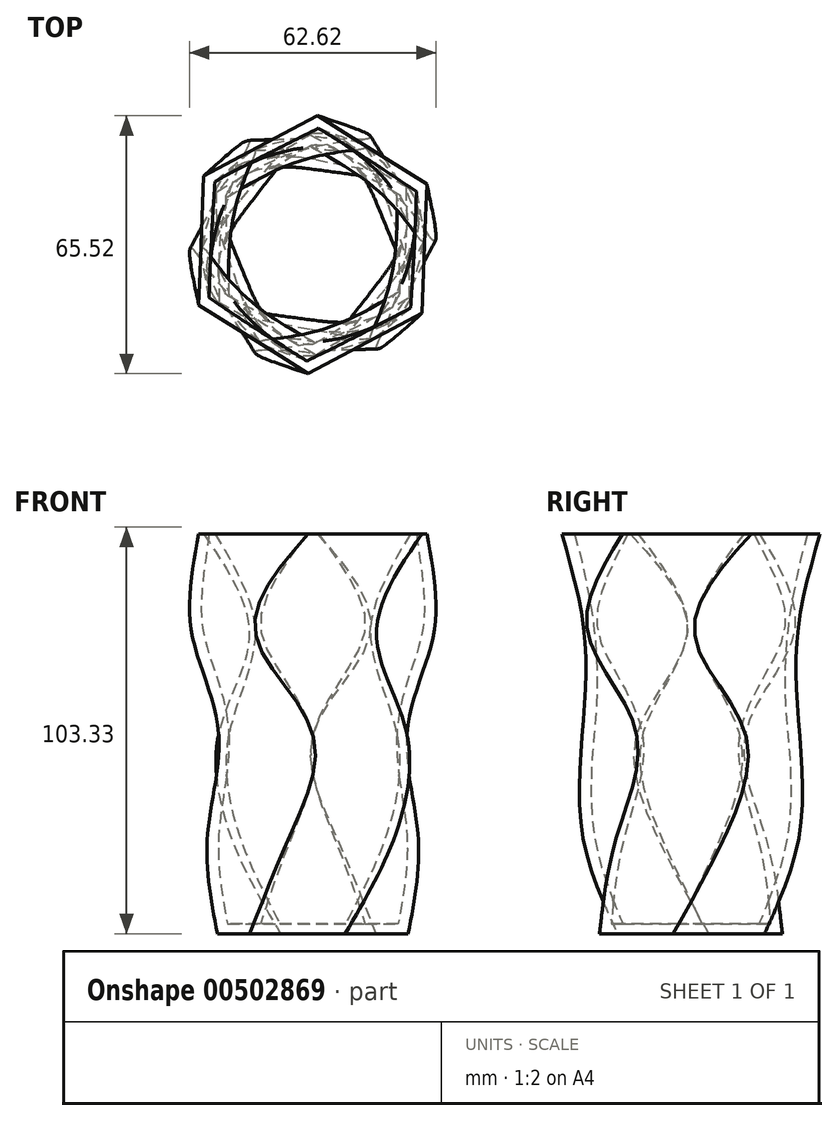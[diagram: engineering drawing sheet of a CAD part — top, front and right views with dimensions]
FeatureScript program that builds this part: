
annotation { "Feature Type Name" : "Feature", "Feature Type Description" : "" }
export const myFeature = defineFeature(function(context is Context, id is Id, definition is map)
    precondition{}
    {
        {
            var Q0;
            Q0=qCreatedBy(makeId("Top.planeOp"),FACE);
            var sketch = newSketch(context, id + "F0", { "sketchPlane" : qUnion([Q0])});
            skCircle(sketch, "E0.cCircle", {"center": v(0, 0) * mm, "radius": 21.33 * mm, "construction": true});
            skLineSegment(sketch, "E0.0", {"start": v(16.04, 18.7) * mm, "end": v(24.2, -4.54) * mm});
            skLineSegment(sketch, "E0.1", {"start": v(24.2, -4.54) * mm, "end": v(8.17, -23.23) * mm});
            skLineSegment(sketch, "E0.2", {"start": v(8.17, -23.23) * mm, "end": v(-16.04, -18.7) * mm});
            skLineSegment(sketch, "E0.3", {"start": v(-16.04, -18.7) * mm, "end": v(-24.2, 4.54) * mm});
            skLineSegment(sketch, "E0.4", {"start": v(-24.2, 4.54) * mm, "end": v(-8.17, 23.23) * mm});
            skLineSegment(sketch, "E0.5", {"start": v(-8.17, 23.23) * mm, "end": v(16.04, 18.7) * mm});
            skPoint(sketch, "E0.0.midPoint", {"position": v(20.12, 7.07) * mm});
            skSolve(sketch);
        }
        {
            var Q0;
            Q0=qCreatedBy(makeId("Top.planeOp"),FACE);
            cPlane(context, id + "F1", {"entities" : qUnion([Q0]), "cplaneType" : CPlaneType.OFFSET, "offset" : 25.4 * mm, "width" : 152.4 * mm, "height" : 152.4 * mm});
        }
        {
            var Q0;
            Q0=qCreatedBy(id+"F1.planeOp",FACE);
            var sketch = newSketch(context, id + "F2", { "sketchPlane" : qUnion([Q0])});
            skCircle(sketch, "E1.cCircle", {"center": v(0, 0) * mm, "radius": 24.38 * mm, "construction": true});
            skLineSegment(sketch, "E1.0", {"start": v(26.7, 8.92) * mm, "end": v(21.08, -18.67) * mm});
            skLineSegment(sketch, "E1.1", {"start": v(21.08, -18.67) * mm, "end": v(-5.63, -27.59) * mm});
            skLineSegment(sketch, "E1.2", {"start": v(-5.63, -27.59) * mm, "end": v(-26.7, -8.92) * mm});
            skLineSegment(sketch, "E1.3", {"start": v(-26.7, -8.92) * mm, "end": v(-21.08, 18.67) * mm});
            skLineSegment(sketch, "E1.4", {"start": v(-21.08, 18.67) * mm, "end": v(5.63, 27.59) * mm});
            skLineSegment(sketch, "E1.5", {"start": v(5.63, 27.59) * mm, "end": v(26.7, 8.92) * mm});
            skPoint(sketch, "E1.0.midPoint", {"position": v(23.9, -4.87) * mm});
            skSolve(sketch);
        }
        {
            var Q0;
            Q0=qCreatedBy(id+"F1.planeOp",FACE);
            cPlane(context, id + "F3", {"entities" : qUnion([Q0]), "cplaneType" : CPlaneType.OFFSET, "offset" : 25.4 * mm, "width" : 152.4 * mm, "height" : 152.4 * mm});
        }
        {
            var Q0;
            Q0=qCreatedBy(id+"F3.planeOp",FACE);
            var sketch = newSketch(context, id + "F4", { "sketchPlane" : qUnion([Q0])});
            skCircle(sketch, "E2.cCircle", {"center": v(0, 0) * mm, "radius": 23.9 * mm, "construction": true});
            skLineSegment(sketch, "E2.0", {"start": v(23.9, 13.8) * mm, "end": v(23.9, -13.8) * mm});
            skLineSegment(sketch, "E2.1", {"start": v(23.9, -13.8) * mm, "end": v(0, -27.59) * mm});
            skLineSegment(sketch, "E2.2", {"start": v(0, -27.59) * mm, "end": v(-23.9, -13.8) * mm});
            skLineSegment(sketch, "E2.3", {"start": v(-23.9, -13.8) * mm, "end": v(-23.9, 13.8) * mm});
            skLineSegment(sketch, "E2.4", {"start": v(-23.9, 13.8) * mm, "end": v(0, 27.59) * mm});
            skLineSegment(sketch, "E2.5", {"start": v(0, 27.59) * mm, "end": v(23.9, 13.8) * mm});
            skPoint(sketch, "E2.0.midPoint", {"position": v(23.9, 0) * mm});
            skSolve(sketch);
        }
        {
            var Q0;
            Q0=qCreatedBy(id+"F3.planeOp",FACE);
            cPlane(context, id + "F5", {"entities" : qUnion([Q0]), "cplaneType" : CPlaneType.OFFSET, "offset" : 25.4 * mm, "width" : 152.4 * mm, "height" : 152.4 * mm});
        }
        {
            var Q0;
            Q0=qCreatedBy(id+"F5.planeOp",FACE);
            var sketch = newSketch(context, id + "F6", { "sketchPlane" : qUnion([Q0])});
            skCircle(sketch, "E3.cCircle", {"center": v(0, 0) * mm, "radius": 26.6 * mm, "construction": true});
            skLineSegment(sketch, "E3.0", {"start": v(14.56, 27.06) * mm, "end": v(30.71, 0.92) * mm});
            skLineSegment(sketch, "E3.1", {"start": v(30.71, 0.92) * mm, "end": v(16.15, -26.14) * mm});
            skLineSegment(sketch, "E3.2", {"start": v(16.15, -26.14) * mm, "end": v(-14.56, -27.06) * mm});
            skLineSegment(sketch, "E3.3", {"start": v(-14.56, -27.06) * mm, "end": v(-30.71, -0.92) * mm});
            skLineSegment(sketch, "E3.4", {"start": v(-30.71, -0.92) * mm, "end": v(-16.15, 26.14) * mm});
            skLineSegment(sketch, "E3.5", {"start": v(-16.15, 26.14) * mm, "end": v(14.56, 27.06) * mm});
            skPoint(sketch, "E3.0.midPoint", {"position": v(22.64, 13.99) * mm});
            skSolve(sketch);
        }
        {
            var Q0;
            Q0=qCreatedBy(id+"F5.planeOp",FACE);
            cPlane(context, id + "F7", {"entities" : qUnion([Q0]), "cplaneType" : CPlaneType.OFFSET, "offset" : 25.4 * mm, "width" : 152.4 * mm, "height" : 152.4 * mm});
        }
        {
            var Q0;
            Q0=qCreatedBy(id+"F7.planeOp",FACE);
            var sketch = newSketch(context, id + "F8", { "sketchPlane" : qUnion([Q0])});
            skCircle(sketch, "E4.cCircle", {"center": v(0, 0) * mm, "radius": 28.4 * mm, "construction": true});
            skLineSegment(sketch, "E4.0", {"start": v(1.2, 32.76) * mm, "end": v(28.98, 15.34) * mm});
            skLineSegment(sketch, "E4.1", {"start": v(28.98, 15.34) * mm, "end": v(27.77, -17.42) * mm});
            skLineSegment(sketch, "E4.2", {"start": v(27.77, -17.42) * mm, "end": v(-1.2, -32.76) * mm});
            skLineSegment(sketch, "E4.3", {"start": v(-1.2, -32.76) * mm, "end": v(-28.98, -15.34) * mm});
            skLineSegment(sketch, "E4.4", {"start": v(-28.98, -15.34) * mm, "end": v(-27.77, 17.42) * mm});
            skLineSegment(sketch, "E4.5", {"start": v(-27.77, 17.42) * mm, "end": v(1.2, 32.76) * mm});
            skPoint(sketch, "E4.0.midPoint", {"position": v(15.1, 24.05) * mm});
            skSolve(sketch);
        }
        {
            var Q0;
            Q0=makeQuery(id+"F8.imprint","IMPRINT",FACE,{"disambiguationData":[TD([[makeQuery(id+"F8.imprint","IMPRINT",EDGE,{"derivedFrom":sQuery(id+"F8.wireOp",EDGE,"E4.0")}),-1.0]])]});
            var Q1;
            Q1=makeQuery(id+"F6.imprint","IMPRINT",FACE,{"disambiguationData":[TD([[makeQuery(id+"F6.imprint","IMPRINT",EDGE,{"derivedFrom":sQuery(id+"F6.wireOp",EDGE,"E3.0")}),-1.0]])]});
            var Q2;
            Q2=makeQuery(id+"F4.imprint","IMPRINT",FACE,{"disambiguationData":[TD([[makeQuery(id+"F4.imprint","IMPRINT",EDGE,{"derivedFrom":sQuery(id+"F4.wireOp",EDGE,"E2.0")}),-1.0]])]});
            var Q3;
            Q3=makeQuery(id+"F2.imprint","IMPRINT",FACE,{"disambiguationData":[TD([[makeQuery(id+"F2.imprint","IMPRINT",EDGE,{"derivedFrom":sQuery(id+"F2.wireOp",EDGE,"E1.0")}),-1.0]])]});
            var Q4;
            Q4=makeQuery(id+"F0.imprint","IMPRINT",FACE,{"disambiguationData":[TD([[makeQuery(id+"F0.imprint","IMPRINT",EDGE,{"derivedFrom":sQuery(id+"F0.wireOp",EDGE,"E0.0")}),-1.0]])]});
            loft(context, id + "F9", {"sheetProfilesArray" : [{ "sheetProfileEntities" : qUnion([Q0]) }, { "sheetProfileEntities" : qUnion([Q1]) }, { "sheetProfileEntities" : qUnion([Q2]) }, { "sheetProfileEntities" : qUnion([Q3]) }, { "sheetProfileEntities" : qUnion([Q4]) }]});
        }
        {
            var Q0;
            Q0=makeQuery(id+"F9.opLoft","CAP_FACE",FACE,{"disambiguationData":[OSD([makeQuery(id+"F8.imprint","IMPRINT",FACE,{"disambiguationData":[TD([[makeQuery(id+"F8.imprint","IMPRINT",EDGE,{"derivedFrom":sQuery(id+"F8.wireOp",EDGE,"E4.0")}),-1.0]])]})])],"isStart":true});
            shell(context, id + "F10", {"entities" : qUnion([Q0]), "thickness" : 2.54 * mm});
        }
    });
